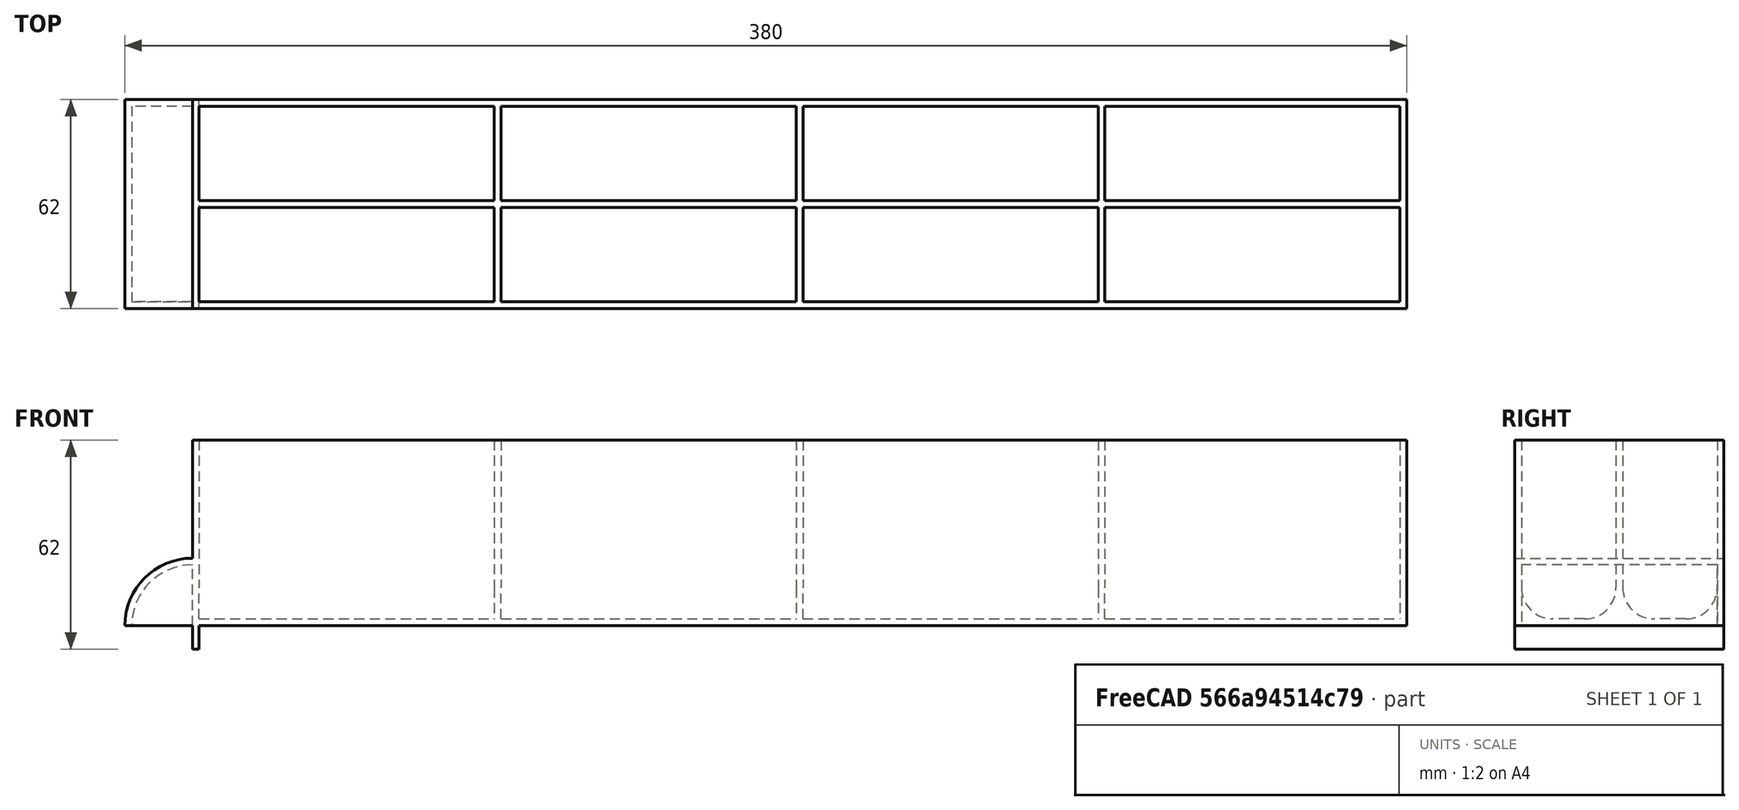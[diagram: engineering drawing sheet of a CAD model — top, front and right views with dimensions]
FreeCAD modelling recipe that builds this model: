
FCSTD DOCUMENT  (FreeCAD 0.19R22960 (Git))
Label: KallaxE24Storage
License: All rights reserved
LicenseURL: http://en.wikipedia.org/wiki/All_rights_reserved
objects: TechDraw::DrawViewDimension×12, Sketcher::SketchObject×4, TechDraw::DrawViewPart×3, PartDesign::Plane×2, PartDesign::Pad×2, PartDesign::LinearPattern×2, TechDraw::DrawViewSection×2, Spreadsheet::Sheet×1, PartDesign::Pocket×1, PartDesign::MultiTransform×1, PartDesign::Revolution×1, PartDesign::Body×1, App::DocumentObjectGroup×1, TechDraw::DrawSVGTemplate×1, TechDraw::DrawPage×1
note: 18 computed .brp shape members not serialized (recipe doc carries the construction recipe); baked Part::Feature solids carry a one-line shape summary decoded from their .brp

FEATURE [Spreadsheet::Sheet] Spreadsheet  label="Daten"
  cells = A2=Umgebung; A3=Zeilen; B3(Zeilen)=5; A4=Spalten; B4(Spalten)=5; A5=Etagen Breite; B5(EtagenBreite)==32cm; A6=Wiederstands Breite; B6(WiederstandsBreite)==65mm; A7=Anzahl an Schubladen; B7(SchubladenAnzahl)==Zeilen * Spalten; A8=Tiefe; B8(MaxTiefe)==36cm; A10=Schublade; D10=Tasche; A11=Schubladen Slack; B11(SchubladenSlack)==2mm; D11=Breite; E11(TaschenBreite)==(SchubladenMaxBreite - (FaecherAnzahlBreite + 1) * Wandstaerke) / FaecherAnzahlBreite; A12=Schublade Max Höhe; B12(SchubladenMaxHoehe)==55mm; D12=Tiefe; E12(TaschenTiefe)==SchubladenMaxHoehe - Wandstaerke; A13=Schublade Max Breite; B13(SchubladenMaxBreite)==EtagenBreite / Spalten - SchubladenSlack; D13=Länge; E13(TaschenLaenge)==(MaxTiefe - (FaecherAnzahlTiefe + 1) * Wandstaerke) / FaecherAnzahlTiefe; A14=Schubladen Overhang; B14(SchubladenOverhang)==7mm; A15=Wanddicke; B15(Wandstaerke)==2mm; A16=Fingereingriff; B16(FingerholeSize)==2cm; A17=Benötigte Fächer; B17=8; A18=Fächer in Breite; B18(FaecherAnzahlBreite)=2; A19=Fächer in Tiefe; B19(FaecherAnzahlTiefe)=4; D19=Grid; D20=Grid Tiefe; E20(GridTiefe)==(TaschenLaenge + Wandstaerke) * (FaecherAnzahlTiefe - 1); D21=Grid Breite; E21(GridBreite)==(TaschenBreite + Wandstaerke) * (FaecherAnzahlBreite - 1); A22=Rundungs Radius; B22(FachrundungRadius)==TaschenBreite / 3
FEATURE [PartDesign::Plane] DatumPlane  label="TopOfBodyPlane"
  AttachmentOffset = pos=(0,0,55) rot=(0,0,1;0rad)
  Length = 421.603
  MapMode = 5
  Placement = pos=(0,0,55) rot=(0,0,1;0rad)
  ResizeMode = 0
  Support = -> [XY_Plane]
  Width = 123.603
  expr: .AttachmentOffset.Base.z = <<Daten>>.SchubladenMaxHoehe
FEATURE [Sketcher::SketchObject] Sketch004  label="FachSkizze"
  MapMode = 5
  Placement = pos=(0,0,55) rot=(0,0,1;0rad)
  Support = -> [DatumPlane]
  expr: Constraints[11] = <<Daten>>.TaschenLaenge
  expr: Constraints[10] = <<Daten>>.TaschenBreite
  expr: Constraints[9] = <<Daten>>.Wandstaerke
  expr: Constraints[8] = <<Daten>>.Wandstaerke
  sketch-geometry (4):
    g0: LineSegment StartX=2 StartY=2 StartZ=0 EndX=89.5 EndY=2 EndZ=0
    g1: LineSegment StartX=89.5 StartY=2 StartZ=0 EndX=89.5 EndY=30 EndZ=0
    g2: LineSegment StartX=89.5 StartY=30 StartZ=0 EndX=2 EndY=30 EndZ=0
    g3: LineSegment StartX=2 StartY=30 StartZ=0 EndX=2 EndY=2 EndZ=0
  constraints (12):
    c: Coincident(g0,g1)
    c: Coincident(g1,g2)
    c: Coincident(g2,g3)
    c: Coincident(g3,g0)
    c: Horizontal(g0)
    c: Horizontal(g2)
    c: Vertical(g1)
    c: Vertical(g3)
    c: DistanceX(g-1,g0) = 2
    c: DistanceY(g-1,g0) = 2
    c: DistanceY(g3,g3) = 28
    c: DistanceX(g2,g2) = 87.5
FEATURE [Sketcher::SketchObject] Sketch006  label="MainBodySketch"
  MapMode = 5
  Placement = pos=(0,0,0) rot=(1,0,0;1.5708rad)
  Support = -> [XZ_Plane]
  expr: Constraints[15] = <<Daten>>.Wandstaerke
  expr: Constraints[11] = <<Daten>>.SchubladenOverhang
  expr: Constraints[10] = <<Daten>>.MaxTiefe
  expr: Constraints[9] = <<Daten>>.SchubladenMaxHoehe
  sketch-geometry (6):
    g0: LineSegment StartX=0 StartY=55 StartZ=0 EndX=360 EndY=55 EndZ=0
    g1: LineSegment StartX=360 StartY=55 StartZ=0 EndX=360 EndY=0 EndZ=0
    g2: LineSegment StartX=360 StartY=0 StartZ=0 EndX=2 EndY=0 EndZ=0
    g3: LineSegment StartX=2 StartY=0 StartZ=0 EndX=2 EndY=-7 EndZ=0
    g4: LineSegment StartX=2 StartY=-7 StartZ=0 EndX=0 EndY=-7 EndZ=0
    g5: LineSegment StartX=0 StartY=-7 StartZ=0 EndX=0 EndY=55 EndZ=0
  constraints (18):
    c: Horizontal(g0)
    c: Coincident(g0,g1)
    c: Vertical(g1)
    c: Coincident(g1,g2)
    c: Horizontal(g2)
    c: Coincident(g2,g3)
    c: Vertical(g3)
    c: Coincident(g3,g4)
    c: Horizontal(g4)
    c: DistanceY(g1,g1) = 55
    c: DistanceX(g0,g0) = 360
    c: DistanceY(g3,g3) = 7
    c: Coincident(g5,g4)
    c: Coincident(g5,g0)
    c: Vertical(g5)
    c: DistanceX(g4,g4) = 2
    c: Vertical(g4,g-1)
    c: Horizontal(g2,g-1)
FEATURE [PartDesign::Pad] Pad002  label="MainBody"
  Direction = (1,1,1)
  Length = 62
  Length2 = 100
  Placement = pos=(0,0,0) rot=(1,0,0;1.5708rad)
  Profile = -> Sketch006
  Refine = true
  Reversed = true
  Type = 0
  expr: Length = <<Daten>>.SchubladenMaxBreite
FEATURE [PartDesign::Pocket] Pocket001  label="Fach"
  BaseFeature = -> Pad002
  Length = 53
  Length2 = 100
  Placement = pos=(0,0,0) rot=(1,0,0;1.5708rad)
  Profile = -> Sketch004
  Refine = true
  Type = 0
  expr: Length = <<Daten>>.TaschenTiefe
FEATURE [PartDesign::Plane] DatumPlane001  label="FachSide"
  AttachmentOffset = pos=(0,0,2) rot=(0,0,1;0rad)
  Length = 103.685
  MapMode = 5
  Placement = pos=(2,-4e-16,4e-16) rot=(0.57735,0.57735,0.57735;2.0944rad)
  ResizeMode = 0
  Support = -> [YZ_Plane]
  Width = 96.6853
  expr: .AttachmentOffset.Base.z = <<Daten>>.Wandstaerke
FEATURE [Sketcher::SketchObject] Sketch  label="FachFiletSketch"
  MapMode = 5
  Placement = pos=(2,-4e-16,4e-16) rot=(0.57735,0.57735,0.57735;2.0944rad)
  Support = -> [DatumPlane001]
  expr: Constraints[14] = <<Daten>>.TaschenBreite
  expr: Constraints[13] = <<Daten>>.Wandstaerke
  expr: Constraints[12] = <<Daten>>.FachrundungRadius
  expr: Constraints[4] = <<Daten>>.FachrundungRadius
  expr: Constraints[3] = <<Daten>>.Wandstaerke
  expr: Constraints[2] = <<Daten>>.Wandstaerke
  sketch-geometry (6):
    g0: ArcOfCircle CenterX=11.3333 CenterY=11.3333 CenterZ=0 NormalX=0 NormalY=0 NormalZ=1 AngleXU=0 Radius=9.33333 StartAngle=3.14159 EndAngle=4.71239
    g1: LineSegment StartX=2 StartY=11.3333 StartZ=0 EndX=2 EndY=2 EndZ=0
    g2: LineSegment StartX=2 StartY=2 StartZ=0 EndX=11.3333 EndY=2 EndZ=0
    g3: ArcOfCircle CenterX=20.6667 CenterY=11.3333 CenterZ=0 NormalX=0 NormalY=0 NormalZ=1 AngleXU=0 Radius=9.33333 StartAngle=4.71239 EndAngle=6.28319
    g4: LineSegment StartX=20.6667 StartY=2 StartZ=0 EndX=30 EndY=2 EndZ=0
    g5: LineSegment StartX=30 StartY=2 StartZ=0 EndX=30 EndY=11.3333 EndZ=0
  constraints (20):
    c: Angle(g0) = 1.5708
    c: Horizontal(g0,g0)
    c: DistanceX(g-1,g0) = 2
    c: DistanceY(g-1,g0) = 2
    c: Radius(g0) = 9.33333
    c: Coincident(g0,g1)
    c: Coincident(g1,g2)
    c: Coincident(g2,g0)
    c: Horizontal(g2)
    c: Vertical(g1)
    c: Horizontal(g3,g3)
    c: Vertical(g3,g3)
    c: Radius(g3) = 9.33333
    c: DistanceY(g-1,g3) = 2
    c: DistanceX(g0,g3) = 28
    c: Coincident(g3,g4)
    c: Coincident(g4,g5)
    c: Coincident(g5,g3)
    c: Vertical(g5)
    c: Horizontal(g4)
FEATURE [PartDesign::Pad] Pad  label="FachFilet"
  BaseFeature = -> Pocket001
  Direction = (1,1,1)
  Length = 87.5
  Length2 = 100
  Placement = pos=(0,0,0) rot=(1,0,0;1.5708rad)
  Profile = -> Sketch
  Refine = true
  Type = 0
  expr: Length = <<Daten>>.TaschenLaenge
FEATURE [PartDesign::LinearPattern] LinearPattern
  Direction = -> Sketch004 [H_Axis]
  Length = 268.5
  Occurrences = 4
  Placement = pos=(0,0,0) rot=(1,0,0;1.5708rad)
  Refine = true
  expr: Occurrences = <<Daten>>.FaecherAnzahlTiefe
  expr: Length = <<Daten>>.GridTiefe
FEATURE [PartDesign::LinearPattern] LinearPattern001
  Direction = -> Sketch004 [V_Axis]
  Length = 30
  Occurrences = 2
  Placement = pos=(0,0,0) rot=(1,0,0;1.5708rad)
  Refine = true
  expr: Occurrences = <<Daten>>.FaecherAnzahlBreite
  expr: Length = <<Daten>>.GridBreite
FEATURE [PartDesign::MultiTransform] MultiTransform
  BaseFeature = -> Pad
  Originals = -> [Pocket001,Pad]
  Placement = pos=(0,0,0) rot=(1,0,0;1.5708rad)
  Refine = true
  Transformations = -> [LinearPattern,LinearPattern001]
FEATURE [Sketcher::SketchObject] Sketch007  label="FingerCatchSketch"
  MapMode = 5
  Placement = pos=(0,0,0) rot=(0.57735,0.57735,0.57735;2.0944rad)
  Support = -> [YZ_Plane]
  expr: Constraints[22] = <<Daten>>.FingerholeSize
  expr: Constraints[21] = <<Daten>>.SchubladenMaxBreite
  expr: Constraints[20] = <<Daten>>.Wandstaerke
  expr: Constraints[19] = <<Daten>>.Wandstaerke
  expr: Constraints[18] = <<Daten>>.Wandstaerke
  sketch-geometry (8):
    g0: LineSegment StartX=0 StartY=0 StartZ=0 EndX=0 EndY=20 EndZ=0
    g1: LineSegment StartX=0 StartY=20 StartZ=0 EndX=62 EndY=20 EndZ=0
    g2: LineSegment StartX=62 StartY=20 StartZ=0 EndX=62 EndY=0 EndZ=0
    g3: LineSegment StartX=62 StartY=0 StartZ=0 EndX=60 EndY=0 EndZ=0
    g4: LineSegment StartX=60 StartY=0 StartZ=0 EndX=60 EndY=18 EndZ=0
    g5: LineSegment StartX=60 StartY=18 StartZ=0 EndX=2 EndY=18 EndZ=0
    g6: LineSegment StartX=2 StartY=18 StartZ=0 EndX=2 EndY=0 EndZ=0
    g7: LineSegment StartX=2 StartY=0 StartZ=0 EndX=0 EndY=0 EndZ=0
  constraints (23):
    c: Coincident(g-1,g0)
    c: PointOnObject(g0,g-2)
    c: Coincident(g0,g1)
    c: Horizontal(g1)
    c: Coincident(g1,g2)
    c: PointOnObject(g2,g-1)
    c: Vertical(g2)
    c: Coincident(g2,g3)
    c: PointOnObject(g3,g-1)
    c: Coincident(g3,g4)
    c: Vertical(g4)
    c: Coincident(g4,g5)
    c: Horizontal(g5)
    c: Coincident(g5,g6)
    c: Vertical(g6)
    c: Coincident(g6,g7)
    c: Coincident(g7,g0)
    c: Horizontal(g7)
    c: DistanceX(g3,g3) = 2
    c: DistanceX(g7,g7) = 2
    c: DistanceY(g4,g1) = 2
    c: DistanceX(g1,g1) = 62
    c: DistanceY(g0,g0) = 20
FEATURE [PartDesign::Revolution] Revolution  label="FingerCatch"
  Angle = 90
  Axis = (3e-16,1,-2e-16)
  Base = (0,0,0)
  BaseFeature = -> MultiTransform
  Placement = pos=(0,0,0) rot=(1,0,0;1.5708rad)
  Profile = -> Sketch007
  ReferenceAxis = -> Sketch007 [H_Axis]
  Refine = true
  Reversed = true
FEATURE [PartDesign::Body] Body  label="Schublade"
  Group = -> [Pad002,DatumPlane,Pocket001,Sketch004,Sketch006,DatumPlane001,Sketch,Pad,MultiTransform,LinearPattern,LinearPattern001,Sketch007,Revolution]
  Origin = -> Origin
  Tip = -> Revolution
FEATURE [App::DocumentObjectGroup] Gruppe
  Group = -> [Body,Spreadsheet]
FEATURE [TechDraw::DrawSVGTemplate] Template
  EditableTexts = Designed_by_Name=Martin Holzhauer; Drawing_number=001; FC-Date=2020-12-19; FC-SC=0,5; FC-SH=1; FC-Title=Kallax Reistor Storage; Subtitle=Subtitle; Weight=-
  Height = 210
  Orientation = 1
  Width = 297
FEATURE [TechDraw::DrawViewPart] View  label="ISO"
  CoarseView = false
  Direction = (-0.577,-0.577,0.577)
  Focus = 100
  HardHidden = false
  IsoCount = 0
  IsoHidden = false
  IsoVisible = false
  LockPosition = false
  Perspective = false
  Rotation = 0
  Scale = 0.2
  ScaleType = 0
  SeamHidden = false
  SeamVisible = true
  SmoothHidden = false
  SmoothVisible = true
  Source = -> [Revolution]
  X = 46.9861
  XDirection = (0.707,-0.707,0)
  Y = 41.7335
FEATURE [TechDraw::DrawViewPart] View002  label="Front"
  CoarseView = false
  Direction = (-1,0,0)
  Focus = 100
  HardHidden = false
  IsoCount = 0
  IsoHidden = false
  IsoVisible = false
  LockPosition = false
  Perspective = false
  Rotation = 0
  Scale = 0.5
  ScaleType = 0
  SeamHidden = false
  SeamVisible = true
  SmoothHidden = false
  SmoothVisible = true
  Source = -> [Revolution]
  X = 37.4154
  XDirection = (0,-1,0)
  Y = 153.775
FEATURE [TechDraw::DrawViewSection] SectionView  label="Längsschnitt"
  BaseView = -> View002
  CoarseView = false
  CutSurfaceDisplay = 2
  Direction = (0,-1,0)
  FileGeomPattern = <userpath>/PortableApps/FreeCAD_0.19.22960-Win-Conda_vc14.x-x86_64/data/Mod/TechDraw/PAT/FCPAT.pat
  FileHatchPattern = <userpath>/PortableApps/FreeCAD_0.19.22960-Win-Conda_vc14.x-x86_64/data/Mod/TechDraw/Patterns/simple.svg
  Focus = 100
  FuseBeforeCut = false
  HardHidden = false
  HatchScale = 1
  IsoCount = 0
  IsoHidden = false
  IsoVisible = false
  LockPosition = false
  NameGeomPattern = Diamant
  Perspective = false
  Rotation = 0
  Scale = 0.5
  ScaleType = 0
  SeamHidden = false
  SeamVisible = true
  SectionDirection = 1
  SectionNormal = (0,-1,0)
  SectionOrigin = (170,17,24)
  SmoothHidden = false
  SmoothVisible = true
  Source = -> [Revolution]
  X = 179.923
  XDirection = (1,0,0)
  Y = 90.9183
FEATURE [TechDraw::DrawViewDimension] Dimension  label="Fachlänge"
  Arbitrary = false
  FormatSpec = %.2f
  Inverted = false
  LockPosition = false
  MeasureType = 1
  OverTolerance = 0
  References2D = -> [SectionView]
  Rotation = 0
  ScaleType = 0
  TheoreticalExact = false
  Type = 1
  UnderTolerance = 0
  X = -41.1083
  Y = 27.3834
FEATURE [TechDraw::DrawViewDimension] Dimension003  label="Finger Catch Innen"
  Arbitrary = false
  FormatSpec = %.2f
  Inverted = false
  LockPosition = false
  MeasureType = 1
  OverTolerance = 0
  References2D = -> [SectionView]
  Rotation = 0
  ScaleType = 0
  TheoreticalExact = false
  Type = 1
  UnderTolerance = 0
  X = -53.7
  Y = -15.5604
FEATURE [TechDraw::DrawViewDimension] Dimension004  label="Breite"
  Arbitrary = false
  FormatSpec = %.2f
  Inverted = false
  LockPosition = false
  MeasureType = 1
  OverTolerance = 0
  References2D = -> [View002]
  Rotation = 0
  ScaleType = 0
  TheoreticalExact = false
  Type = 1
  UnderTolerance = 0
  X = 0.621944
  Y = 44.0608
FEATURE [TechDraw::DrawViewPart] View003  label="Seite"
  CoarseView = false
  Direction = (0,-1,0)
  Focus = 100
  HardHidden = false
  IsoCount = 0
  IsoHidden = false
  IsoVisible = false
  LockPosition = false
  Perspective = false
  Rotation = 0
  Scale = 0.5
  ScaleType = 0
  SeamHidden = false
  SeamVisible = true
  SmoothHidden = false
  SmoothVisible = true
  Source = -> [Revolution]
  X = 182.288
  XDirection = (1,0,0)
  Y = 154.133
FEATURE [TechDraw::DrawViewSection] SectionView001  label="Querschnitt"
  BaseView = -> View003
  CoarseView = false
  CutSurfaceDisplay = 2
  Direction = (1,0,0)
  FileGeomPattern = <userpath>/PortableApps/FreeCAD_0.19.22960-Win-Conda_vc14.x-x86_64/data/Mod/TechDraw/PAT/FCPAT.pat
  FileHatchPattern = <userpath>/PortableApps/FreeCAD_0.19.22960-Win-Conda_vc14.x-x86_64/data/Mod/TechDraw/Patterns/simple.svg
  Focus = 100
  FuseBeforeCut = false
  HardHidden = false
  HatchScale = 1
  IsoCount = 0
  IsoHidden = false
  IsoVisible = false
  LockPosition = false
  NameGeomPattern = Diamant
  Perspective = false
  Rotation = 0
  Scale = 0.5
  ScaleType = 0
  SeamHidden = false
  SeamVisible = true
  SectionDirection = 1
  SectionNormal = (1,0,0)
  SectionOrigin = (170,75,24)
  SmoothHidden = false
  SmoothVisible = true
  Source = -> [Revolution]
  X = 40.3977
  XDirection = (0,1,0)
  Y = 91.7384
FEATURE [TechDraw::DrawViewDimension] Dimension005  label="Länge"
  Arbitrary = false
  FormatSpec = %.2f
  Inverted = false
  LockPosition = false
  MeasureType = 1
  OverTolerance = 0
  References2D = -> [View003]
  Rotation = 0
  ScaleType = 0
  TheoreticalExact = false
  Type = 1
  UnderTolerance = 0
  X = 5.73655
  Y = 28.9206
FEATURE [TechDraw::DrawViewDimension] Dimension006  label="Höhe"
  Arbitrary = false
  FormatSpec = %.2f
  Inverted = false
  LockPosition = false
  MeasureType = 1
  OverTolerance = 0
  References2D = -> [View003]
  Rotation = 0
  ScaleType = 0
  TheoreticalExact = false
  Type = 2
  UnderTolerance = 0
  X = 61.3536
  Y = 0.801223
FEATURE [TechDraw::DrawViewDimension] Dimension007  label="Fachhöhe"
  Arbitrary = false
  FormatSpec = %.2f
  Inverted = false
  LockPosition = false
  MeasureType = 1
  OverTolerance = 0
  References2D = -> [SectionView001]
  Rotation = 0
  ScaleType = 0
  TheoreticalExact = false
  Type = 2
  UnderTolerance = 0
  X = -28.5758
  Y = 1.55472
FEATURE [TechDraw::DrawViewDimension] Dimension008  label="Fachbreite"
  Arbitrary = false
  FormatSpec = %.2f
  Inverted = false
  LockPosition = false
  MeasureType = 1
  OverTolerance = 0
  References2D = -> [SectionView001]
  Rotation = 0
  ScaleType = 0
  TheoreticalExact = false
  Type = 1
  UnderTolerance = 0
  X = -22.1116
  Y = 23.7158
FEATURE [TechDraw::DrawViewDimension] Dimension009  label="Wandstärke"
  Arbitrary = false
  FormatSpec = %.2f
  Inverted = false
  LockPosition = false
  MeasureType = 1
  OverTolerance = 0
  References2D = -> [SectionView001]
  Rotation = 0
  ScaleType = 0
  TheoreticalExact = false
  Type = 1
  UnderTolerance = 0
  X = 23.5657
  Y = 22.6181
FEATURE [TechDraw::DrawViewDimension] Dimension010  label="Überhang Länge"
  Arbitrary = false
  FormatSpec = %.2f
  Inverted = false
  LockPosition = false
  MeasureType = 1
  OverTolerance = 0
  References2D = -> [View002]
  Rotation = 0
  ScaleType = 0
  TheoreticalExact = false
  Type = 2
  UnderTolerance = 0
  X = 28.9522
  Y = -26.4875
FEATURE [TechDraw::DrawViewDimension] Dimension011  label="Finger Catch Aussen"
  Arbitrary = false
  FormatSpec = %.2f
  Inverted = false
  LockPosition = false
  MeasureType = 1
  OverTolerance = 0
  References2D = -> [View002]
  Rotation = 0
  ScaleType = 0
  TheoreticalExact = false
  Type = 2
  UnderTolerance = 0
  X = 21.6061
  Y = 5.71212
FEATURE [TechDraw::DrawViewDimension] Dimension012  label="Fillet Radius"
  Arbitrary = false
  FormatSpec = R%.2f
  Inverted = false
  LockPosition = false
  MeasureType = 1
  OverTolerance = 0
  References2D = -> [SectionView001]
  Rotation = 0
  ScaleType = 0
  TheoreticalExact = false
  Type = 4
  UnderTolerance = 0
  X = 24.1858
  Y = -0.228168
FEATURE [TechDraw::DrawViewDimension] Dimension013
  Arbitrary = false
  FormatSpec = %.2f
  Inverted = false
  LockPosition = false
  MeasureType = 1
  OverTolerance = 0
  References2D = -> [View003]
  Rotation = 0
  ScaleType = 0
  TheoreticalExact = false
  Type = 1
  UnderTolerance = 0
  X = -75.4772
  Y = -15.3155
FEATURE [TechDraw::DrawPage] Page
  KeepUpdated = true
  NextBalloonIndex = 1
  ProjectionType = 0
  Template = -> Template
  Views = -> [View,View002,SectionView,Dimension,Dimension003,Dimension004,View003,SectionView001,Dimension005,Dimension006,Dimension007,Dimension008,Dimension009,Dimension010,Dimension011,Dimension012,Dimension013]
